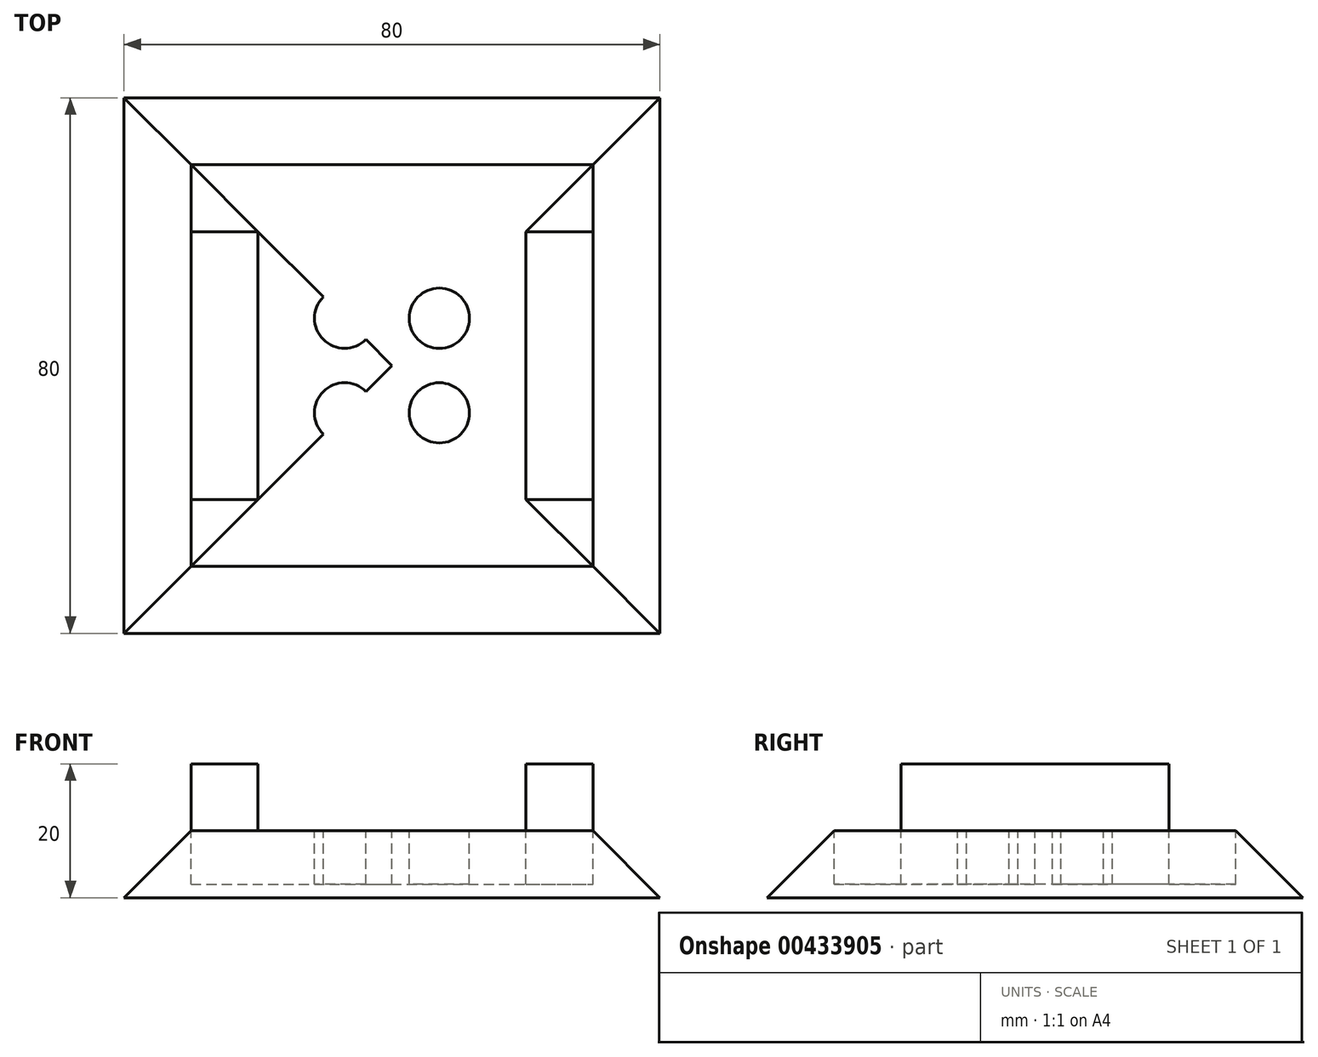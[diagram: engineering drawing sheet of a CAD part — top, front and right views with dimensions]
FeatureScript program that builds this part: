
annotation { "Feature Type Name" : "Feature", "Feature Type Description" : "" }
export const myFeature = defineFeature(function(context is Context, id is Id, definition is map)
    precondition{}
    {
        {
            var Q0;
            Q0=qCreatedBy(makeId("Top.planeOp"),FACE);
            var sketch = newSketch(context, id + "F0", { "sketchPlane" : qUnion([Q0])});
            skLineSegment(sketch, "E0.bottom", {"start": v(-40, 40) * mm, "end": v(40, 40) * mm});
            skLineSegment(sketch, "E0.top", {"start": v(-40, -40) * mm, "end": v(40, -40) * mm});
            skLineSegment(sketch, "E0.left", {"start": v(-40, 40) * mm, "end": v(-40, -40) * mm});
            skLineSegment(sketch, "E0.right", {"start": v(40, 40) * mm, "end": v(40, -40) * mm});
            skSolve(sketch);
        }
        {
            var Q0;
            Q0=makeQuery(id+"F0.imprint","IMPRINT",FACE,{"disambiguationData":[TD([[makeQuery(id+"F0.imprint","IMPRINT",EDGE,{"derivedFrom":sQuery(id+"F0.wireOp",EDGE,"E0.bottom")}),-1.0]])]});
            extrude(context, id + "F1", {"entities" : qUnion([Q0]), "depth" : 10 * mm});
        }
        {
            var Q0;
            Q0=makeQuery(id+"F1.opExtrude","CAP_FACE",FACE,{"disambiguationData":[OSD([sQuery(id+"F0.wireOp",EDGE,"E0.bottom"),sQuery(id+"F0.wireOp",EDGE,"E0.top"),sQuery(id+"F0.wireOp",EDGE,"E0.left"),sQuery(id+"F0.wireOp",EDGE,"E0.right")])],"isStart":false});
            chamfer(context, id + "F2", {"entities" : qUnion([Q0]), "chamferType" : ChamferType.OFFSET_ANGLE, "width" : 10 * mm, "oppositeDirection" : false, "angle" : 45 * degree, "tangentPropagation" : true});
        }
        {
            var Q0;
            Q0=makeQuery(id+"F1.opExtrude","CAP_FACE",FACE,{"disambiguationData":[OSD([sQuery(id+"F0.wireOp",EDGE,"E0.bottom"),sQuery(id+"F0.wireOp",EDGE,"E0.top"),sQuery(id+"F0.wireOp",EDGE,"E0.left"),sQuery(id+"F0.wireOp",EDGE,"E0.right")])],"isStart":false});
            var sketch = newSketch(context, id + "F3", { "sketchPlane" : qUnion([Q0])});
            skLineSegment(sketch, "E1.bottom", {"start": v(-30, 20) * mm, "end": v(-20, 20) * mm});
            skLineSegment(sketch, "E1.top", {"start": v(-30, -20) * mm, "end": v(-20, -20) * mm});
            skLineSegment(sketch, "E1.left", {"start": v(-30, 20) * mm, "end": v(-30, -20) * mm});
            skLineSegment(sketch, "E1.right", {"start": v(-20, 20) * mm, "end": v(-20, -20) * mm});
            skLineSegment(sketch, "E2.bottom", {"start": v(30, 20) * mm, "end": v(20, 20) * mm});
            skLineSegment(sketch, "E2.top", {"start": v(30, -20) * mm, "end": v(20, -20) * mm});
            skLineSegment(sketch, "E2.left", {"start": v(30, 20) * mm, "end": v(30, -20) * mm});
            skLineSegment(sketch, "E2.right", {"start": v(20, 20) * mm, "end": v(20, -20) * mm});
            skSolve(sketch);
        }
        {
            var Q0;
            Q0=makeQuery(id+"F3.imprint","IMPRINT",FACE,{"disambiguationData":[TD([[makeQuery(id+"F3.imprint","IMPRINT",EDGE,{"derivedFrom":sQuery(id+"F3.wireOp",EDGE,"E2.bottom")}),1.0]])]});
            var Q1;
            Q1=makeQuery(id+"F3.imprint","IMPRINT",FACE,{"disambiguationData":[TD([[makeQuery(id+"F3.imprint","IMPRINT",EDGE,{"derivedFrom":sQuery(id+"F3.wireOp",EDGE,"E1.bottom")}),-1.0]])]});
            extrude(context, id + "F4", {"entities" : qUnion([Q0, Q1]), "operationType" : NewBodyOperationType.ADD, "depth" : 10 * mm});
        }
        {
            var Q0;
            Q0=makeQuery(id+"F1.opExtrude","CAP_FACE",FACE,{"disambiguationData":[OSD([sQuery(id+"F0.wireOp",EDGE,"E0.bottom"),sQuery(id+"F0.wireOp",EDGE,"E0.top"),sQuery(id+"F0.wireOp",EDGE,"E0.left"),sQuery(id+"F0.wireOp",EDGE,"E0.right")])],"isStart":false});
            var sketch = newSketch(context, id + "F5", { "sketchPlane" : qUnion([Q0])});
            skLineSegment(sketch, "E3", {"start": v(-30, 30) * mm, "end": v(30, -30) * mm});
            skLineSegment(sketch, "E4", {"start": v(-30, -30) * mm, "end": v(30, 30) * mm});
            skCircle(sketch, "E5", {"center": v(-7.07, 7.07) * mm, "radius": 4.5 * mm});
            skCircle(sketch, "E6.MirrorC", {"center": v(7.07, 7.07) * mm, "radius": 4.5 * mm});
            skCircle(sketch, "E7.MirrorC", {"center": v(-7.07, -7.07) * mm, "radius": 4.5 * mm});
            skCircle(sketch, "E8.MirrorC", {"center": v(7.07, -7.07) * mm, "radius": 4.5 * mm});
            skSolve(sketch);
        }
        {
            var Q0;
            {var subQ0=sQuery(id+"F5.wireOp",EDGE,"E7.MirrorC");var subQ1=sQuery(id+"F5.wireOp",EDGE,"E4");var subQ2=makeQuery(id+"F5.imprint","INTERSECT",VERTEX,{"disambiguationData":[OD(0.0)],"derivedFrom":[subQ1,subQ0]});Q0=makeQuery(id+"F5.imprint","IMPRINT",FACE,{"disambiguationData":[TD([[makeQuery(id+"F5.imprint","IMPRINT",EDGE,{"disambiguationData":[TD([[subQ2,-1.0]])],"derivedFrom":subQ1}),-1.0]])]});}
            var Q1;
            {var subQ0=sQuery(id+"F5.wireOp",EDGE,"E6.MirrorC");var subQ1=sQuery(id+"F5.wireOp",EDGE,"E4");var subQ2=makeQuery(id+"F5.imprint","INTERSECT",VERTEX,{"disambiguationData":[OD(0.0)],"derivedFrom":[subQ1,subQ0]});Q1=makeQuery(id+"F5.imprint","IMPRINT",FACE,{"disambiguationData":[TD([[makeQuery(id+"F5.imprint","IMPRINT",EDGE,{"disambiguationData":[TD([[subQ2,-1.0]])],"derivedFrom":subQ1}),1.0]])]});}
            var Q2;
            {var subQ0=sQuery(id+"F5.wireOp",EDGE,"E5");var subQ1=sQuery(id+"F5.wireOp",EDGE,"E3");var subQ2=makeQuery(id+"F5.imprint","INTERSECT",VERTEX,{"disambiguationData":[OD(0.0)],"derivedFrom":[subQ1,subQ0]});Q2=makeQuery(id+"F5.imprint","IMPRINT",FACE,{"disambiguationData":[TD([[makeQuery(id+"F5.imprint","IMPRINT",EDGE,{"disambiguationData":[TD([[subQ2,-1.0]])],"derivedFrom":subQ1}),1.0]])]});}
            var Q3;
            {var subQ0=sQuery(id+"F5.wireOp",EDGE,"E6.MirrorC");var subQ1=sQuery(id+"F5.wireOp",EDGE,"E4");var subQ2=makeQuery(id+"F5.imprint","INTERSECT",VERTEX,{"disambiguationData":[OD(0.0)],"derivedFrom":[subQ1,subQ0]});Q3=makeQuery(id+"F5.imprint","IMPRINT",FACE,{"disambiguationData":[TD([[makeQuery(id+"F5.imprint","IMPRINT",EDGE,{"disambiguationData":[TD([[subQ2,-1.0]])],"derivedFrom":subQ1}),-1.0]])]});}
            var Q4;
            {var subQ0=sQuery(id+"F5.wireOp",EDGE,"E8.MirrorC");var subQ1=sQuery(id+"F5.wireOp",EDGE,"E3");var subQ2=makeQuery(id+"F5.imprint","INTERSECT",VERTEX,{"disambiguationData":[OD(0.0)],"derivedFrom":[subQ1,subQ0]});Q4=makeQuery(id+"F5.imprint","IMPRINT",FACE,{"disambiguationData":[TD([[makeQuery(id+"F5.imprint","IMPRINT",EDGE,{"disambiguationData":[TD([[subQ2,-1.0]])],"derivedFrom":subQ1}),-1.0]])]});}
            var Q5;
            {var subQ0=sQuery(id+"F5.wireOp",EDGE,"E5");var subQ1=sQuery(id+"F5.wireOp",EDGE,"E3");var subQ2=makeQuery(id+"F5.imprint","INTERSECT",VERTEX,{"disambiguationData":[OD(0.0)],"derivedFrom":[subQ1,subQ0]});Q5=makeQuery(id+"F5.imprint","IMPRINT",FACE,{"disambiguationData":[TD([[makeQuery(id+"F5.imprint","IMPRINT",EDGE,{"disambiguationData":[TD([[subQ2,-1.0]])],"derivedFrom":subQ1}),-1.0]])]});}
            var Q6;
            {var subQ0=sQuery(id+"F5.wireOp",EDGE,"E7.MirrorC");var subQ1=sQuery(id+"F5.wireOp",EDGE,"E4");var subQ2=makeQuery(id+"F5.imprint","INTERSECT",VERTEX,{"disambiguationData":[OD(0.0)],"derivedFrom":[subQ1,subQ0]});Q6=makeQuery(id+"F5.imprint","IMPRINT",FACE,{"disambiguationData":[TD([[makeQuery(id+"F5.imprint","IMPRINT",EDGE,{"disambiguationData":[TD([[subQ2,-1.0]])],"derivedFrom":subQ1}),1.0]])]});}
            var Q7;
            {var subQ0=sQuery(id+"F5.wireOp",EDGE,"E8.MirrorC");var subQ1=sQuery(id+"F5.wireOp",EDGE,"E3");var subQ2=makeQuery(id+"F5.imprint","INTERSECT",VERTEX,{"disambiguationData":[OD(0.0)],"derivedFrom":[subQ1,subQ0]});Q7=makeQuery(id+"F5.imprint","IMPRINT",FACE,{"disambiguationData":[TD([[makeQuery(id+"F5.imprint","IMPRINT",EDGE,{"disambiguationData":[TD([[subQ2,-1.0]])],"derivedFrom":subQ1}),1.0]])]});}
            extrude(context, id + "F6", {"entities" : qUnion([Q0, Q1, Q2, Q3, Q4, Q5, Q6, Q7]), "operationType" : NewBodyOperationType.REMOVE, "oppositeDirection" : true, "depth" : 8 * mm});
        }
    });
